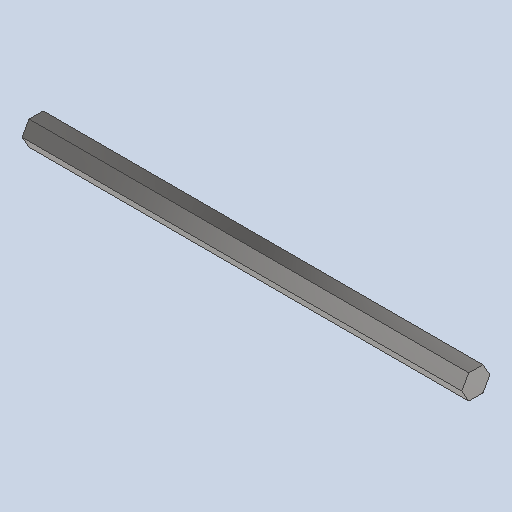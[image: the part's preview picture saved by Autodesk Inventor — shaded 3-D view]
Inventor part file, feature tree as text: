
AUTODESK INVENTOR PART (.ipt)
format: ipt  version: 2023 (Build 270158000, 158)  size: 88,576 bytes
history: native  units: in
note: dims shown in document units (in); Inventor stores cm internally (conversion verified against a paired STEP export)
features: other x3, sketch x1
ambient origin geometry x8: Origin, YZ Plane, XZ Plane, XY Plane, X Axis, Y Axis, Z Axis, Center Point
bodies: Solid1 (feature_tree)
feature tree (4):
  other  "9in-0.5inHexAxel.ipt"
  other  "Solid1::9in-0.5inHexAxel.ipt"
  other  "TaggingFeature1"
  sketch  "Sketch1"  dims[d0=0.3937in]
